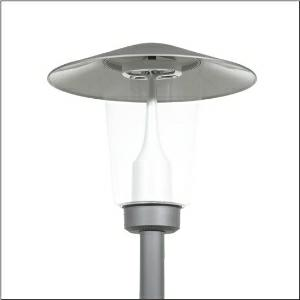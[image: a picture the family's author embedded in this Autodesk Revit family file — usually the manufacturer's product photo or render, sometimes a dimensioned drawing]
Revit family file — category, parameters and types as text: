
# Revit family: pilzleuchte_iq___st1_2a_5xa5235ef14hp_2efb
name_source: partatom
category: Lighting Fixtures
units: mm (PartAtom-declared; Revit-internal decimal feet)

## family parameters
Cut with Voids When Loaded = No
Host = Face
Light Source = No
Part Type = Normal
Room Calculation Point = No
Round Connector Dimension = Use Diameter
Shared = No

## types (1)
- --- (1 x LED, 4770 lm, 33.6 W, 3000K)
    Apparent Load = 34 VA
    CIE Flux Codes = 23 60 92 98 100
    Color Rendering = 70
    Color Temperature = 3000K
    Default Elevation = 1800 mm
    Description = Mushroom Luminaire iQ, mast luminaire, Module 540 iQ-SR, primary light control with 3 zone facetted reflector, of plastic, silver coated, highly specular, structured, primary optical cover: cover, of PMMA, transparent, light distribution: ST1.2a, light emission: direct distribution, primary light characteristic: asymmetric, installation type: post-top, LED, High Power LED, rated luminous flux: 4.770lm, luminous efficacy: 142lm/W, light colour: 730, colour temperature: 3000K, control gear: iQ Street-Remote, control: pre-setting: logarithmic dimming characteristic, Street-Remote, Auto-Match, Temp-Guard, Lumen-Switch, Night-Set, Smart-Wire, Light-Fading, Desk-Remote (wireless, voltage-free reading and setting of iQ features in the workshop via application-optimized NFC function/RFID function), optimised constant luminous flux control (CLO 2.0), with terminal, 6-pole, max. 2.5mm², mains connection: 230..240V, AC, 50/60Hz, start of lifetime: 34W, end of service life: 36W, reduction: 15W, luminaire housing, upper part, of glass-fibre reinforced polyester, coated, Siteco® metallic grey (DB 702S), diameter: 650mm, height: 586mm, spigot size: d x l = 76 x 70mm (post-top) | with reducer (optional accessory) 60 x 70mm, mounting height: 3..5m, post-top mast mounting element, of diecast aluminium, coated, Siteco® metallic grey (DB 702S), Module 540 iQ-SR, traffic white (RAL 9016), equipment: Power, protection rating (complete): IP65, insulation class (complete): insulation class II (safety insulation), certification: CE, ENEC, VDE, packaging unit: 1 piece

Light Distribution: ST1.2a
    Height = 586 mm
    Lamp = 1 x LED
    Lamp Light Flux = 4770 lm
    Lamp Power = 33.6 W
    Lamp count = 1
    Length = 650 mm
    Luminous efficacy = 142 lm/W
    Manufacturer = Siteco
    ModVariant = No
    Model = 5XA5235EF14HP
    Number of Poles = 1
    OnlyDefault = Yes
    Power Factor = 1
    Product Name = Pilzleuchte iQ | ST1.2a
    Product group = mast luminaire | pylon top
    ProductGroupID = 6100
    Protection Class = Protection class II
    Protection Degree = IP 65
    RLX_Detail_Level = 1
    RLX_Emergency_Light_Flux = 0 lm
    RLX_Emergency_Type = 0
    RLX_Emergency_Type_DB = No
    RlxData = <blob elided: 51513 chars, md5=f0feb3e5>
    Socket = socket
    Standby Power = 0 W
    System Light Flux = 4770 lm
    System Power = 34 W
    Type Comments = factory setting: luminous flux: 100 % | dim-lin: 254 | 695 mA
    Type Image = l_1006077.jpg
    URL = http://relux.com
    VarID = @adj_214921
    Voltage = 0 V
    Weight = 0.00 kg
    Width = 0 mm  [stored 0 ft]

note: [stored X ft] marks values corroborated as IEEE doubles in the binary element streams (Revit-internal decimal feet)

## geometry (parser evidence)
native form markers: Blend x4, Sweep x13
no freeform markers — native parametric forms only
